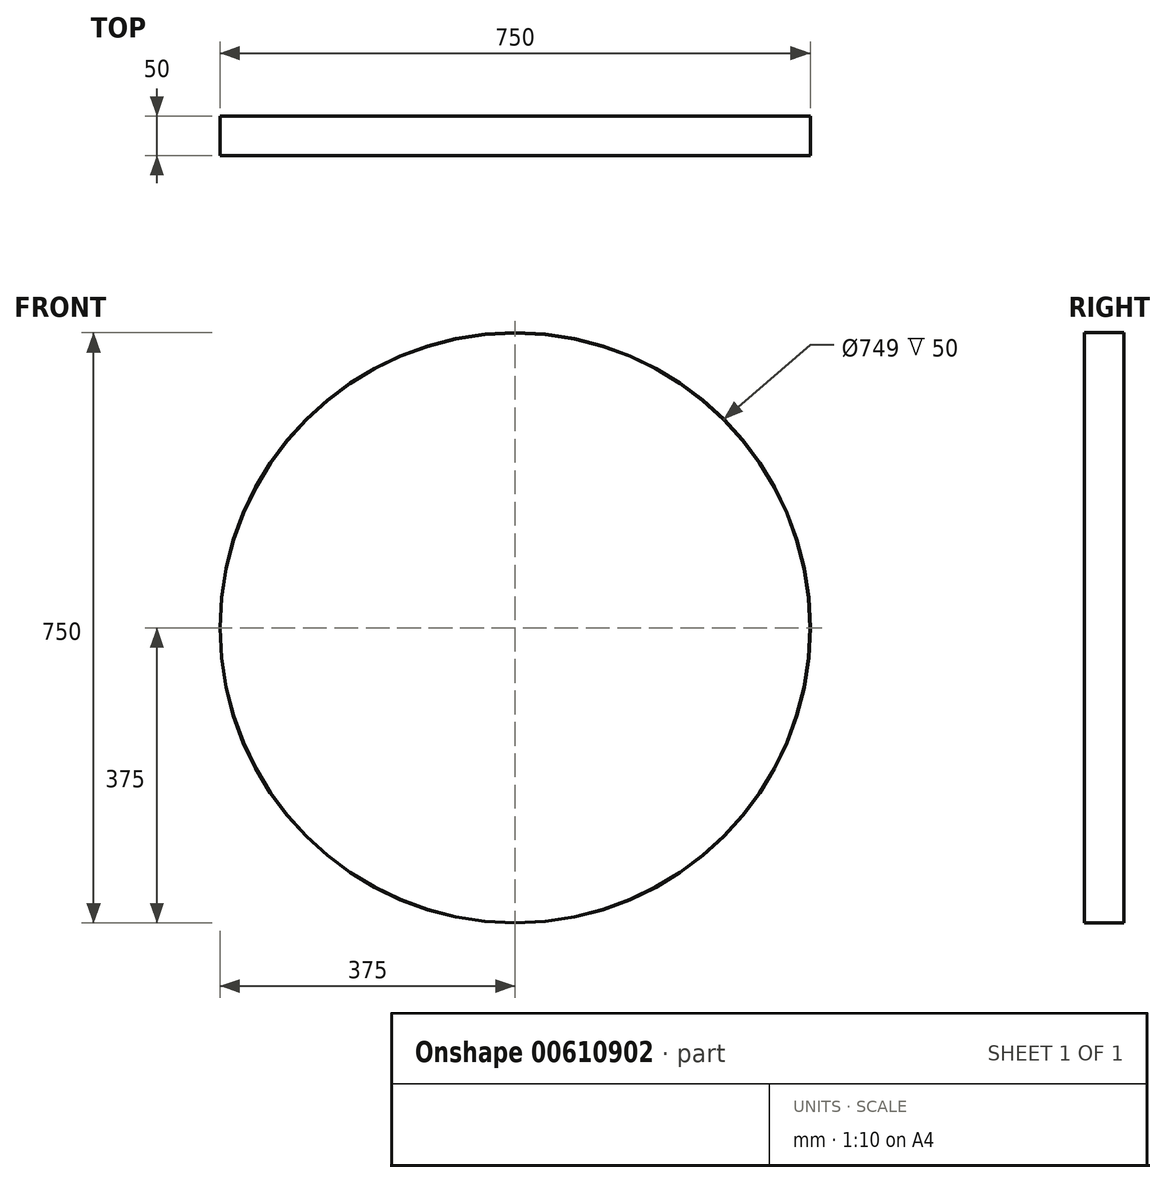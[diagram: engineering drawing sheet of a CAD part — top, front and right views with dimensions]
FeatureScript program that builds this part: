
annotation { "Feature Type Name" : "Feature", "Feature Type Description" : "" }
export const myFeature = defineFeature(function(context is Context, id is Id, definition is map)
    precondition{}
    {
        {
            var Q0;
            Q0=qCreatedBy(makeId("Front.planeOp"),FACE);
            var sketch = newSketch(context, id + "F0", { "sketchPlane" : qUnion([Q0])});
            skCircle(sketch, "E0", {"center": v(0, 0) * mm, "radius": 375 * mm});
            skCircle(sketch, "E1", {"center": v(0, 0) * mm, "radius": 374.5 * mm});
            skSolve(sketch);
        }
        {
            var Q0;
            Q0=makeQuery(id+"F0.imprint","IMPRINT",FACE,{"disambiguationData":[TD([[makeQuery(id+"F0.imprint","IMPRINT",EDGE,{"derivedFrom":sQuery(id+"F0.wireOp",EDGE,"E0")}),1.0]])]});
            extrude(context, id + "F1", {"entities" : qUnion([Q0]), "depth" : 50 * mm, "offsetDistance" : 25 * mm});
        }
    });
